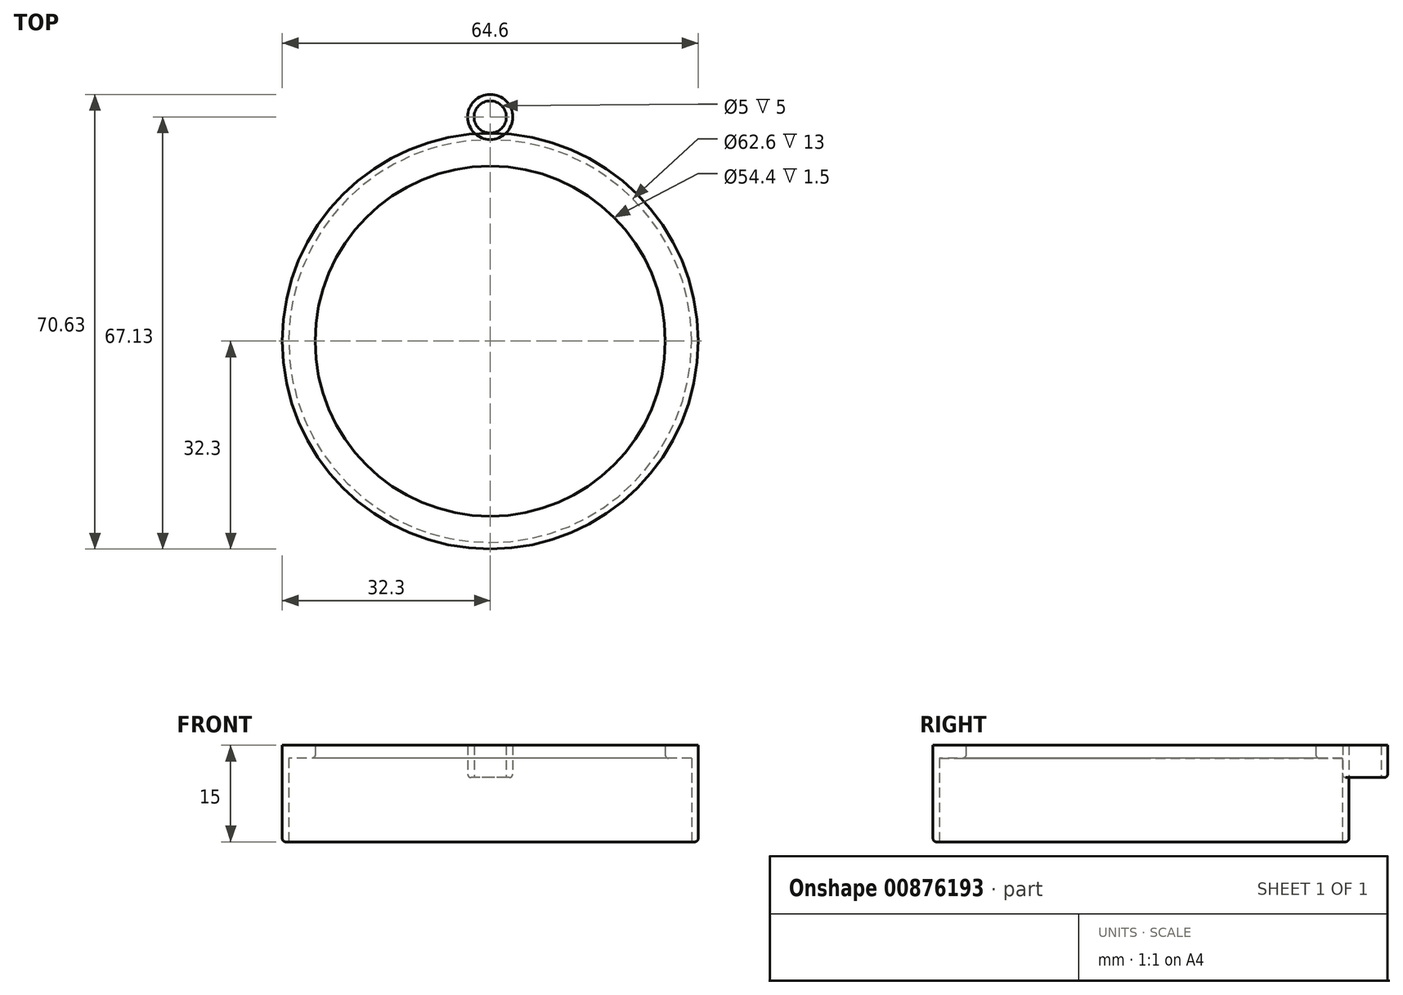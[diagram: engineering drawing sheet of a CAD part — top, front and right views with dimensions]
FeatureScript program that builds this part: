
annotation { "Feature Type Name" : "Feature", "Feature Type Description" : "" }
export const myFeature = defineFeature(function(context is Context, id is Id, definition is map)
    precondition{}
    {
        {
            var Q0;
            Q0=qCreatedBy(makeId("Top.planeOp"),FACE);
            var sketch = newSketch(context, id + "F0", { "sketchPlane" : qUnion([Q0])});
            skCircle(sketch, "E0", {"center": v(0, 0) * mm, "radius": 32.3 * mm});
            skSolve(sketch);
        }
        {
            var Q0;
            Q0 = qSketchRegion(id + "F0", true);
            extrude(context, id + "F1", {"entities" : qUnion([Q0]), "depth" : 15 * mm, "offsetDistance" : 25 * mm});
        }
        {
            var Q0;
            Q0=qCreatedBy(makeId("Top.planeOp"),FACE);
            var sketch = newSketch(context, id + "F2", { "sketchPlane" : qUnion([Q0])});
            skCircle(sketch, "E1", {"center": v(0, 0) * mm, "radius": 31.3 * mm});
            skSolve(sketch);
        }
        {
            var Q0;
            Q0=makeQuery(id+"F2.imprint","IMPRINT",FACE,{"disambiguationData":[TD([[makeQuery(id+"F2.imprint","IMPRINT",EDGE,{"derivedFrom":sQuery(id+"F2.wireOp",EDGE,"E1")}),1.0]])]});
            var Q1;
            Q1=sQuery(id+"F2.wireOp",EDGE,"E1");
            extrude(context, id + "F3", {"entities" : qUnion([Q0]), "operationType" : NewBodyOperationType.REMOVE, "surfaceEntities" : qUnion([Q1]), "depth" : 13 * mm, "offsetDistance" : 25 * mm});
        }
        {
            var Q0;
            Q0=qCreatedBy(makeId("Top.planeOp"),FACE);
            var sketch = newSketch(context, id + "F4", { "sketchPlane" : qUnion([Q0])});
            skCircle(sketch, "E2", {"center": v(0, 0) * mm, "radius": 27.2 * mm});
            skSolve(sketch);
        }
        {
            var Q0;
            Q0 = qSketchRegion(id + "F4", true);
            extrude(context, id + "F5", {"entities" : qUnion([Q0]), "operationType" : NewBodyOperationType.REMOVE, "depth" : 15 * mm, "offsetDistance" : 25 * mm});
        }
        {
            var Q0;
            Q0=qCreatedBy(makeId("Top.planeOp"),FACE);
            var sketch = newSketch(context, id + "F6", { "sketchPlane" : qUnion([Q0])});
            skCircle(sketch, "E3", {"center": v(0, 0) * mm, "radius": 3.5 * mm});
            skSolve(sketch);
        }
        {
            var Q0;
            Q0 = qSketchRegion(id + "F6", true);
            extrude(context, id + "F7", {"entities" : qUnion([Q0]), "depth" : 5 * mm, "offsetDistance" : 25 * mm});
        }
        {
            var Q0;
            Q0=qCreatedBy(makeId("Top.planeOp"),FACE);
            var sketch = newSketch(context, id + "F8", { "sketchPlane" : qUnion([Q0])});
            skCircle(sketch, "E4", {"center": v(0, 0) * mm, "radius": 2.5 * mm});
            skSolve(sketch);
        }
        {
            var Q0;
            Q0 = qSketchRegion(id + "F8", true);
            extrude(context, id + "F9", {"entities" : qUnion([Q0]), "operationType" : NewBodyOperationType.REMOVE, "depth" : 5 * mm, "offsetDistance" : 25 * mm});
        }
        {
            var Q0;
            Q0=makeQuery(id+"F7.opExtrude","SWEPT_BODY",BODY,{"disambiguationData":[OSD([sQuery(id+"F6.wireOp",EDGE,"E3")])]});
            transform(context, id + "F10", {"entities" : qUnion([Q0]), "transformType" : TransformType.TRANSLATION_3D, "dx" : 0 * mm, "dy" : 34.6 * mm, "dz" : 0 * mm, "makeCopy" : false});
        }
        {
            var Q0;
            Q0=makeQuery(id+"F7.opExtrude","SWEPT_BODY",BODY,{"disambiguationData":[OSD([sQuery(id+"F6.wireOp",EDGE,"E3")])]});
            transform(context, id + "F11", {"entities" : qUnion([Q0]), "transformType" : TransformType.TRANSLATION_3D, "dx" : 0 * mm, "dy" : 0.23 * mm, "dz" : 0 * mm, "makeCopy" : false});
        }
        {
            var Q0;
            Q0=makeQuery(id+"F5.boolean.opBoolean","INTERSECT",EDGE,{"derivedFrom":[makeQuery(id+"F3.boolean.opBoolean","COPY",FACE,{"derivedFrom":makeQuery(id+"F3.opExtrude","CAP_FACE",FACE,{"disambiguationData":[OSD([sQuery(id+"F2.wireOp",EDGE,"E1")])],"isStart":false})}),makeQuery(id+"F5.opExtrude","SWEPT_FACE",FACE,{"disambiguationData":[OSD([sQuery(id+"F4.wireOp",EDGE,"E2")])]})]});
            var Q1;
            Q1=makeQuery(id+"F3.boolean.opBoolean","COPY",EDGE,{"derivedFrom":makeQuery(id+"F3.opExtrude","CAP_EDGE",EDGE,{"disambiguationData":[OSD([sQuery(id+"F2.wireOp",EDGE,"E1")])],"isStart":true})});
            var Q2;
            Q2=makeQuery(id+"F1.opExtrude","CAP_EDGE",EDGE,{"disambiguationData":[OSD([sQuery(id+"F0.wireOp",EDGE,"E0")])],"isStart":true});
            var Q3;
            Q3=makeQuery(id+"F9.boolean.opBoolean","COPY",EDGE,{"derivedFrom":makeQuery(id+"F9.opExtrude","CAP_EDGE",EDGE,{"disambiguationData":[OSD([sQuery(id+"F8.wireOp",EDGE,"E4")])],"isStart":true})});
            var Q4;
            Q4=makeQuery(id+"F7.opExtrude","CAP_EDGE",EDGE,{"disambiguationData":[OSD([sQuery(id+"F6.wireOp",EDGE,"E3")])],"isStart":true});
            fillet(context, id + "F12", {"entities" : qUnion([Q0, Q1, Q2, Q3, Q4]), "radius" : 0.5 * mm, "tangentPropagation" : true, "allowEdgeOverflow" : false});
        }
        {
            var Q0;
            Q0=makeQuery(id+"F7.opExtrude","SWEPT_BODY",BODY,{"disambiguationData":[OSD([sQuery(id+"F6.wireOp",EDGE,"E3")])]});
            transform(context, id + "F13", {"entities" : qUnion([Q0]), "transformType" : TransformType.TRANSLATION_3D, "dx" : 0 * mm, "dy" : 0 * mm, "dz" : 10 * mm, "makeCopy" : false});
        }
    });
